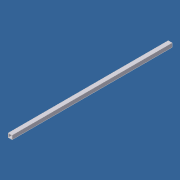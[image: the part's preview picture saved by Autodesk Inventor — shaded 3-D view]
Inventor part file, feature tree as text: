
AUTODESK INVENTOR PART (.ipt)
format: ipt  version: 2012 (Build 160160000, 160)  size: 70,144 bytes
history: native  units: in
note: dims shown in document units (in); Inventor stores cm internally (conversion verified against a paired STEP export)
features: extrude x1, sketch x1
ambient origin geometry x8: Origin, YZ Plane, XZ Plane, XY Plane, X Axis, Y Axis, Z Axis, Center Point
bodies: Solid1 (feature_tree)
feature tree (2):
  extrude  "Extrusion1"  Depth=1.75in
  sketch  "Sketch1"  dims[d0=0.125in d1=1.75in d2=71.0in d3=0.0in]
